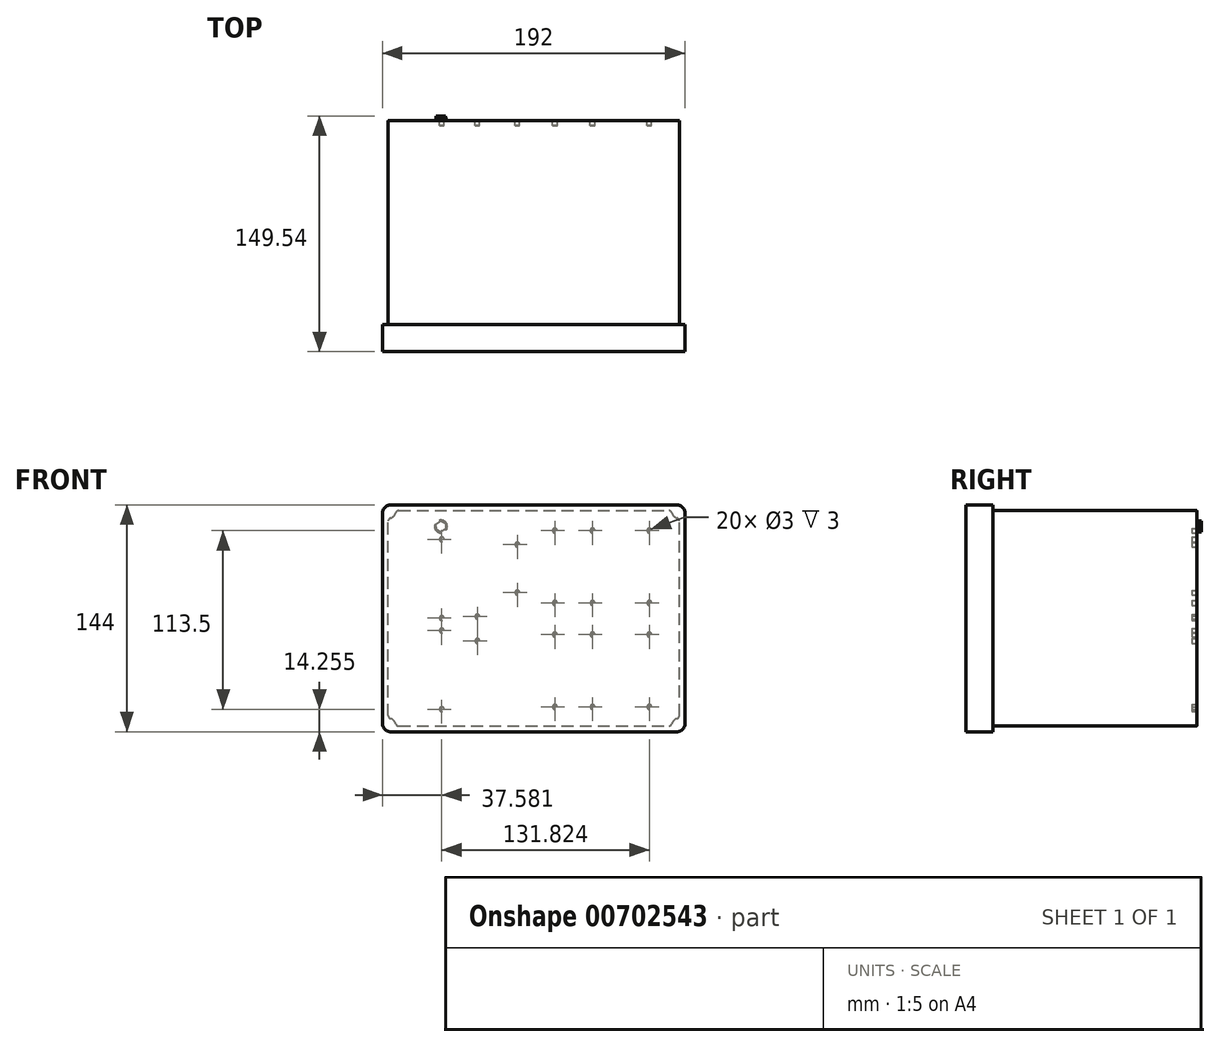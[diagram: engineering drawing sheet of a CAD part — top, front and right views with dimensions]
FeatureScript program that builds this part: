
annotation { "Feature Type Name" : "Feature", "Feature Type Description" : "" }
export const myFeature = defineFeature(function(context is Context, id is Id, definition is map)
    precondition{}
    {
        {
            var Q0;
            Q0=qCreatedBy(makeId("Front.planeOp"),FACE);
            var sketch = newSketch(context, id + "F0", { "sketchPlane" : qUnion([Q0])});
            skLineSegment(sketch, "E0.bottom", {"start": v(96, -72) * mm, "end": v(-96, -72) * mm});
            skLineSegment(sketch, "E0.top", {"start": v(96, 72) * mm, "end": v(-96, 72) * mm});
            skLineSegment(sketch, "E0.left", {"start": v(96, -72) * mm, "end": v(96, 72) * mm});
            skLineSegment(sketch, "E0.right", {"start": v(-96, -72) * mm, "end": v(-96, 72) * mm});
            skPoint(sketch, "E0.middle", {"position": v(0, 0) * mm});
            skSolve(sketch);
        }
        {
            var Q0;
            Q0 = qSketchRegion(id + "F0", true);
            extrude(context, id + "F1", {"entities" : qUnion([Q0]), "depth" : 17 * mm, "offsetDistance" : 25 * mm});
        }
        {
            var Q0;
            Q0=makeQuery(id+"F1.opExtrude","CAP_FACE",FACE,{"disambiguationData":[OSD([sQuery(id+"F0.wireOp",EDGE,"E0.bottom"),sQuery(id+"F0.wireOp",EDGE,"E0.top"),sQuery(id+"F0.wireOp",EDGE,"E0.left"),sQuery(id+"F0.wireOp",EDGE,"E0.right")])],"isStart":true});
            var sketch = newSketch(context, id + "F2", { "sketchPlane" : qUnion([Q0])});
            skLineSegment(sketch, "E1.bottom", {"start": v(92.46, -68.45) * mm, "end": v(-92.45, -68.46) * mm});
            skLineSegment(sketch, "E1.top", {"start": v(92.45, 68.46) * mm, "end": v(-92.45, 68.45) * mm});
            skLineSegment(sketch, "E1.left", {"start": v(92.45, -68.45) * mm, "end": v(92.45, 68.46) * mm});
            skLineSegment(sketch, "E1.right", {"start": v(-92.45, -68.46) * mm, "end": v(-92.45, 68.45) * mm});
            skPoint(sketch, "E1.middle", {"position": v(0, 0) * mm});
            skCircle(sketch, "E2", {"center": v(-92.45, 68.45) * mm, "radius": 5 * mm});
            skCircle(sketch, "E3", {"center": v(92.45, 68.46) * mm, "radius": 5 * mm});
            skCircle(sketch, "E4", {"center": v(92.46, -68.45) * mm, "radius": 5 * mm});
            skCircle(sketch, "E5", {"center": v(-92.45, -68.46) * mm, "radius": 5 * mm});
            skSolve(sketch);
        }
        {
            var Q0;
            {var subQ10=sQuery(id+"F2.wireOp",EDGE,"E4");var subQ13=sQuery(id+"F2.wireOp",EDGE,"E1.bottom");var subQ14=makeQuery(id+"F2.imprint","INTERSECT",VERTEX,{"derivedFrom":[subQ13,subQ10]});Q0=makeQuery(id+"F2.imprint","IMPRINT",FACE,{"disambiguationData":[TD([[makeQuery(id+"F2.imprint","IMPRINT",EDGE,{"disambiguationData":[TD([[subQ14,-1.0]])],"derivedFrom":subQ13}),-1.0]])]});}
            extrude(context, id + "F3", {"entities" : qUnion([Q0]), "operationType" : NewBodyOperationType.ADD, "depth" : 129.54 * mm, "offsetDistance" : 25 * mm});
        }
        {
            var Q0;
            Q0=makeQuery(id+"F3.opExtrude","SWEPT_EDGE",EDGE,{"disambiguationData":[OSD([sQuery(id+"F2.wireOp",EDGE,"E1.top"),sQuery(id+"F2.wireOp",EDGE,"E3")])]});
            var Q1;
            Q1=makeQuery(id+"F3.opExtrude","SWEPT_EDGE",EDGE,{"disambiguationData":[OSD([sQuery(id+"F2.wireOp",EDGE,"E1.left"),sQuery(id+"F2.wireOp",EDGE,"E3")])]});
            var Q2;
            Q2=makeQuery(id+"F3.opExtrude","SWEPT_EDGE",EDGE,{"disambiguationData":[OSD([sQuery(id+"F2.wireOp",EDGE,"E1.left"),sQuery(id+"F2.wireOp",EDGE,"E4")])]});
            var Q3;
            Q3=makeQuery(id+"F3.opExtrude","SWEPT_EDGE",EDGE,{"disambiguationData":[OSD([sQuery(id+"F2.wireOp",EDGE,"E1.bottom"),sQuery(id+"F2.wireOp",EDGE,"E4")])]});
            var Q4;
            Q4=makeQuery(id+"F3.opExtrude","SWEPT_EDGE",EDGE,{"disambiguationData":[OSD([sQuery(id+"F2.wireOp",EDGE,"E1.bottom"),sQuery(id+"F2.wireOp",EDGE,"E5")])]});
            var Q5;
            Q5=makeQuery(id+"F3.opExtrude","SWEPT_EDGE",EDGE,{"disambiguationData":[OSD([sQuery(id+"F2.wireOp",EDGE,"E1.right"),sQuery(id+"F2.wireOp",EDGE,"E5")])]});
            var Q6;
            Q6=makeQuery(id+"F3.opExtrude","SWEPT_EDGE",EDGE,{"disambiguationData":[OSD([sQuery(id+"F2.wireOp",EDGE,"E1.right"),sQuery(id+"F2.wireOp",EDGE,"E2")])]});
            var Q7;
            Q7=makeQuery(id+"F3.opExtrude","SWEPT_EDGE",EDGE,{"disambiguationData":[OSD([sQuery(id+"F2.wireOp",EDGE,"E1.top"),sQuery(id+"F2.wireOp",EDGE,"E2")])]});
            fillet(context, id + "F4", {"entities" : qUnion([Q0, Q1, Q2, Q3, Q4, Q5, Q6, Q7]), "radius" : 2 * mm, "tangentPropagation" : true, "allowEdgeOverflow" : false});
        }
        {
            var Q0;
            Q0=makeQuery(id+"F1.opExtrude","SWEPT_EDGE",EDGE,{"disambiguationData":[OSD([sQuery(id+"F0.wireOp",EDGE,"E0.top"),sQuery(id+"F0.wireOp",EDGE,"E0.left")])]});
            var Q1;
            Q1=makeQuery(id+"F1.opExtrude","SWEPT_EDGE",EDGE,{"disambiguationData":[OSD([sQuery(id+"F0.wireOp",EDGE,"E0.top"),sQuery(id+"F0.wireOp",EDGE,"E0.right")])]});
            var Q2;
            Q2=makeQuery(id+"F1.opExtrude","SWEPT_EDGE",EDGE,{"disambiguationData":[OSD([sQuery(id+"F0.wireOp",EDGE,"E0.bottom"),sQuery(id+"F0.wireOp",EDGE,"E0.right")])]});
            var Q3;
            Q3=makeQuery(id+"F1.opExtrude","SWEPT_EDGE",EDGE,{"disambiguationData":[OSD([sQuery(id+"F0.wireOp",EDGE,"E0.bottom"),sQuery(id+"F0.wireOp",EDGE,"E0.left")])]});
            fillet(context, id + "F5", {"entities" : qUnion([Q0, Q1, Q2, Q3]), "radius" : 5 * mm, "tangentPropagation" : true, "allowEdgeOverflow" : false});
        }
        {
            var Q0;
            Q0=makeQuery(id+"F3.opExtrude","CAP_FACE",FACE,{"disambiguationData":[OSD([sQuery(id+"F2.wireOp",EDGE,"E1.bottom"),sQuery(id+"F2.wireOp",EDGE,"E1.top"),sQuery(id+"F2.wireOp",EDGE,"E1.left"),sQuery(id+"F2.wireOp",EDGE,"E1.right"),sQuery(id+"F2.wireOp",EDGE,"E2"),sQuery(id+"F2.wireOp",EDGE,"E3"),sQuery(id+"F2.wireOp",EDGE,"E4"),sQuery(id+"F2.wireOp",EDGE,"E5")])],"isStart":false});
            var sketch = newSketch(context, id + "F6", { "sketchPlane" : qUnion([Q0])});
            skCircle(sketch, "E6", {"center": v(58.95, 58.3) * mm, "radius": 4.06 * mm});
            skCircle(sketch, "E7.cCircle", {"center": v(58.95, 58.3) * mm, "radius": 3 * mm, "construction": true});
            skLineSegment(sketch, "E7.0", {"start": v(61.9, 56.47) * mm, "end": v(58.85, 54.83) * mm});
            skLineSegment(sketch, "E7.1", {"start": v(58.85, 54.83) * mm, "end": v(55.9, 56.66) * mm});
            skLineSegment(sketch, "E7.2", {"start": v(55.9, 56.66) * mm, "end": v(56.01, 60.12) * mm});
            skLineSegment(sketch, "E7.3", {"start": v(56.01, 60.12) * mm, "end": v(59.06, 61.76) * mm});
            skLineSegment(sketch, "E7.4", {"start": v(59.06, 61.76) * mm, "end": v(62, 59.93) * mm});
            skLineSegment(sketch, "E7.5", {"start": v(62, 59.93) * mm, "end": v(61.9, 56.47) * mm});
            skPoint(sketch, "E7.0.midPoint", {"position": v(60.37, 55.65) * mm});
            skCircle(sketch, "E8", {"center": v(-73.4, 55.75) * mm, "radius": 1.5 * mm});
            skCircle(sketch, "E9", {"center": v(-37.34, 55.76) * mm, "radius": 1.5 * mm});
            skCircle(sketch, "E10", {"center": v(-13.46, 55.76) * mm, "radius": 1.5 * mm});
            skCircle(sketch, "E11.0.1.0", {"center": v(-73.4, 9.78) * mm, "radius": 1.5 * mm});
            skCircle(sketch, "E11.0.1.1", {"center": v(-37.34, 9.78) * mm, "radius": 1.5 * mm});
            skCircle(sketch, "E11.0.1.2", {"center": v(-13.46, 9.78) * mm, "radius": 1.5 * mm});
            skLineSegment(sketch, "E11.direction1", {"start": v(-73.4, 55.75) * mm, "end": v(-48.4, 55.75) * mm, "construction": true});
            skLineSegment(sketch, "E11.direction2", {"start": v(-73.4, 55.75) * mm, "end": v(-73.4, 9.78) * mm, "construction": true});
            skCircle(sketch, "E12.0.1.0", {"center": v(-73.4, -10.29) * mm, "radius": 1.5 * mm});
            skLineSegment(sketch, "E12.0.1.1", {"start": v(-73.4, -10.29) * mm, "end": v(-73.4, -56.26) * mm, "construction": true});
            skLineSegment(sketch, "E12.0.1.2", {"start": v(-73.4, -10.29) * mm, "end": v(-48.4, -10.29) * mm, "construction": true});
            skCircle(sketch, "E12.0.1.3", {"center": v(-13.46, -56.26) * mm, "radius": 1.5 * mm});
            skCircle(sketch, "E12.0.1.4", {"center": v(-37.34, -10.28) * mm, "radius": 1.5 * mm});
            skCircle(sketch, "E12.0.1.5", {"center": v(-13.46, -10.28) * mm, "radius": 1.5 * mm});
            skCircle(sketch, "E12.0.1.6", {"center": v(-73.4, -56.26) * mm, "radius": 1.5 * mm});
            skCircle(sketch, "E12.0.1.7", {"center": v(-37.34, -56.26) * mm, "radius": 1.5 * mm});
            skLineSegment(sketch, "E12.direction1", {"start": v(-73.4, 9.78) * mm, "end": v(-48.4, 9.78) * mm, "construction": true});
            skLineSegment(sketch, "E12.direction2", {"start": v(-73.4, 9.78) * mm, "end": v(-73.4, -56.26) * mm, "construction": true});
            skCircle(sketch, "E13", {"center": v(10.41, 46.87) * mm, "radius": 1.5 * mm});
            skCircle(sketch, "E14", {"center": v(10.41, 16.39) * mm, "radius": 1.5 * mm});
            skCircle(sketch, "E15", {"center": v(58.42, 50.17) * mm, "radius": 1.5 * mm});
            skCircle(sketch, "E16", {"center": v(58.42, 0.17) * mm, "radius": 1.5 * mm});
            skCircle(sketch, "E17.0.1.0", {"center": v(58.42, -7.74) * mm, "radius": 1.5 * mm});
            skCircle(sketch, "E17.0.1.1", {"center": v(58.42, -57.74) * mm, "radius": 1.5 * mm});
            skLineSegment(sketch, "E17.direction1", {"start": v(58.42, 0.17) * mm, "end": v(83.42, 0.17) * mm, "construction": true});
            skLineSegment(sketch, "E17.direction2", {"start": v(58.42, 0.17) * mm, "end": v(58.42, -57.74) * mm, "construction": true});
            skCircle(sketch, "E18", {"center": v(35.81, 1.14) * mm, "radius": 1.5 * mm});
            skCircle(sketch, "E19", {"center": v(35.81, -14.35) * mm, "radius": 1.5 * mm});
            skSolve(sketch);
        }
        {
            var Q0;
            Q0=makeQuery(id+"F6.imprint","IMPRINT",FACE,{"disambiguationData":[TD([[makeQuery(id+"F6.imprint","IMPRINT",EDGE,{"derivedFrom":sQuery(id+"F6.wireOp",EDGE,"E8")}),1.0]])]});
            var Q1;
            Q1=makeQuery(id+"F6.imprint","IMPRINT",FACE,{"disambiguationData":[TD([[makeQuery(id+"F6.imprint","IMPRINT",EDGE,{"derivedFrom":sQuery(id+"F6.wireOp",EDGE,"E9")}),1.0]])]});
            var Q2;
            Q2=makeQuery(id+"F6.imprint","IMPRINT",FACE,{"disambiguationData":[TD([[makeQuery(id+"F6.imprint","IMPRINT",EDGE,{"derivedFrom":sQuery(id+"F6.wireOp",EDGE,"E10")}),1.0]])]});
            var Q3;
            Q3=makeQuery(id+"F6.imprint","IMPRINT",FACE,{"disambiguationData":[TD([[makeQuery(id+"F6.imprint","IMPRINT",EDGE,{"derivedFrom":sQuery(id+"F6.wireOp",EDGE,"E11.0.1.0")}),1.0]])]});
            var Q4;
            Q4=makeQuery(id+"F6.imprint","IMPRINT",FACE,{"disambiguationData":[TD([[makeQuery(id+"F6.imprint","IMPRINT",EDGE,{"derivedFrom":sQuery(id+"F6.wireOp",EDGE,"E11.0.1.1")}),1.0]])]});
            var Q5;
            Q5=makeQuery(id+"F6.imprint","IMPRINT",FACE,{"disambiguationData":[TD([[makeQuery(id+"F6.imprint","IMPRINT",EDGE,{"derivedFrom":sQuery(id+"F6.wireOp",EDGE,"E11.0.1.2")}),1.0]])]});
            var Q6;
            Q6=makeQuery(id+"F6.imprint","IMPRINT",FACE,{"disambiguationData":[TD([[makeQuery(id+"F6.imprint","IMPRINT",EDGE,{"derivedFrom":sQuery(id+"F6.wireOp",EDGE,"E12.0.1.0")}),1.0]])]});
            var Q7;
            Q7=makeQuery(id+"F6.imprint","IMPRINT",FACE,{"disambiguationData":[TD([[makeQuery(id+"F6.imprint","IMPRINT",EDGE,{"derivedFrom":sQuery(id+"F6.wireOp",EDGE,"E12.0.1.3")}),1.0]])]});
            var Q8;
            Q8=makeQuery(id+"F6.imprint","IMPRINT",FACE,{"disambiguationData":[TD([[makeQuery(id+"F6.imprint","IMPRINT",EDGE,{"derivedFrom":sQuery(id+"F6.wireOp",EDGE,"E12.0.1.4")}),1.0]])]});
            var Q9;
            Q9=makeQuery(id+"F6.imprint","IMPRINT",FACE,{"disambiguationData":[TD([[makeQuery(id+"F6.imprint","IMPRINT",EDGE,{"derivedFrom":sQuery(id+"F6.wireOp",EDGE,"E12.0.1.5")}),1.0]])]});
            var Q10;
            Q10=makeQuery(id+"F6.imprint","IMPRINT",FACE,{"disambiguationData":[TD([[makeQuery(id+"F6.imprint","IMPRINT",EDGE,{"derivedFrom":sQuery(id+"F6.wireOp",EDGE,"E12.0.1.6")}),1.0]])]});
            var Q11;
            Q11=makeQuery(id+"F6.imprint","IMPRINT",FACE,{"disambiguationData":[TD([[makeQuery(id+"F6.imprint","IMPRINT",EDGE,{"derivedFrom":sQuery(id+"F6.wireOp",EDGE,"E12.0.1.7")}),1.0]])]});
            var Q12;
            Q12=makeQuery(id+"F6.imprint","IMPRINT",FACE,{"disambiguationData":[TD([[makeQuery(id+"F6.imprint","IMPRINT",EDGE,{"derivedFrom":sQuery(id+"F6.wireOp",EDGE,"E13")}),1.0]])]});
            var Q13;
            Q13=makeQuery(id+"F6.imprint","IMPRINT",FACE,{"disambiguationData":[TD([[makeQuery(id+"F6.imprint","IMPRINT",EDGE,{"derivedFrom":sQuery(id+"F6.wireOp",EDGE,"E14")}),1.0]])]});
            var Q14;
            Q14=makeQuery(id+"F6.imprint","IMPRINT",FACE,{"disambiguationData":[TD([[makeQuery(id+"F6.imprint","IMPRINT",EDGE,{"derivedFrom":sQuery(id+"F6.wireOp",EDGE,"E15")}),1.0]])]});
            var Q15;
            Q15=makeQuery(id+"F6.imprint","IMPRINT",FACE,{"disambiguationData":[TD([[makeQuery(id+"F6.imprint","IMPRINT",EDGE,{"derivedFrom":sQuery(id+"F6.wireOp",EDGE,"E16")}),1.0]])]});
            var Q16;
            Q16=makeQuery(id+"F6.imprint","IMPRINT",FACE,{"disambiguationData":[TD([[makeQuery(id+"F6.imprint","IMPRINT",EDGE,{"derivedFrom":sQuery(id+"F6.wireOp",EDGE,"E17.0.1.0")}),1.0]])]});
            var Q17;
            Q17=makeQuery(id+"F6.imprint","IMPRINT",FACE,{"disambiguationData":[TD([[makeQuery(id+"F6.imprint","IMPRINT",EDGE,{"derivedFrom":sQuery(id+"F6.wireOp",EDGE,"E17.0.1.1")}),1.0]])]});
            var Q18;
            Q18=makeQuery(id+"F6.imprint","IMPRINT",FACE,{"disambiguationData":[TD([[makeQuery(id+"F6.imprint","IMPRINT",EDGE,{"derivedFrom":sQuery(id+"F6.wireOp",EDGE,"E18")}),1.0]])]});
            var Q19;
            Q19=makeQuery(id+"F6.imprint","IMPRINT",FACE,{"disambiguationData":[TD([[makeQuery(id+"F6.imprint","IMPRINT",EDGE,{"derivedFrom":sQuery(id+"F6.wireOp",EDGE,"E19")}),1.0]])]});
            extrude(context, id + "F7", {"entities" : qUnion([Q0, Q1, Q2, Q3, Q4, Q5, Q6, Q7, Q8, Q9, Q10, Q11, Q12, Q13, Q14, Q15, Q16, Q17, Q18, Q19]), "operationType" : NewBodyOperationType.REMOVE, "oppositeDirection" : true, "depth" : 3 * mm, "offsetDistance" : 25 * mm});
        }
        {
            var Q0;
            Q0=makeQuery(id+"F6.imprint","IMPRINT",FACE,{"disambiguationData":[TD([[makeQuery(id+"F6.imprint","IMPRINT",EDGE,{"derivedFrom":sQuery(id+"F6.wireOp",EDGE,"E6")}),1.0]])]});
            var Q1;
            Q1=makeQuery(id+"F6.imprint","IMPRINT",FACE,{"disambiguationData":[TD([[makeQuery(id+"F6.imprint","IMPRINT",EDGE,{"derivedFrom":sQuery(id+"F6.wireOp",EDGE,"E7.0")}),-1.0]])]});
            extrude(context, id + "F8", {"entities" : qUnion([Q0, Q1]), "operationType" : NewBodyOperationType.ADD, "depth" : 1 * mm, "offsetDistance" : 25 * mm});
        }
        {
            var Q0;
            Q0=makeQuery(id+"F6.imprint","IMPRINT",FACE,{"disambiguationData":[TD([[makeQuery(id+"F6.imprint","IMPRINT",EDGE,{"derivedFrom":sQuery(id+"F6.wireOp",EDGE,"E7.0")}),-1.0]])]});
            extrude(context, id + "F9", {"entities" : qUnion([Q0]), "operationType" : NewBodyOperationType.ADD, "depth" : 3 * mm, "offsetDistance" : 25 * mm});
        }
    });
